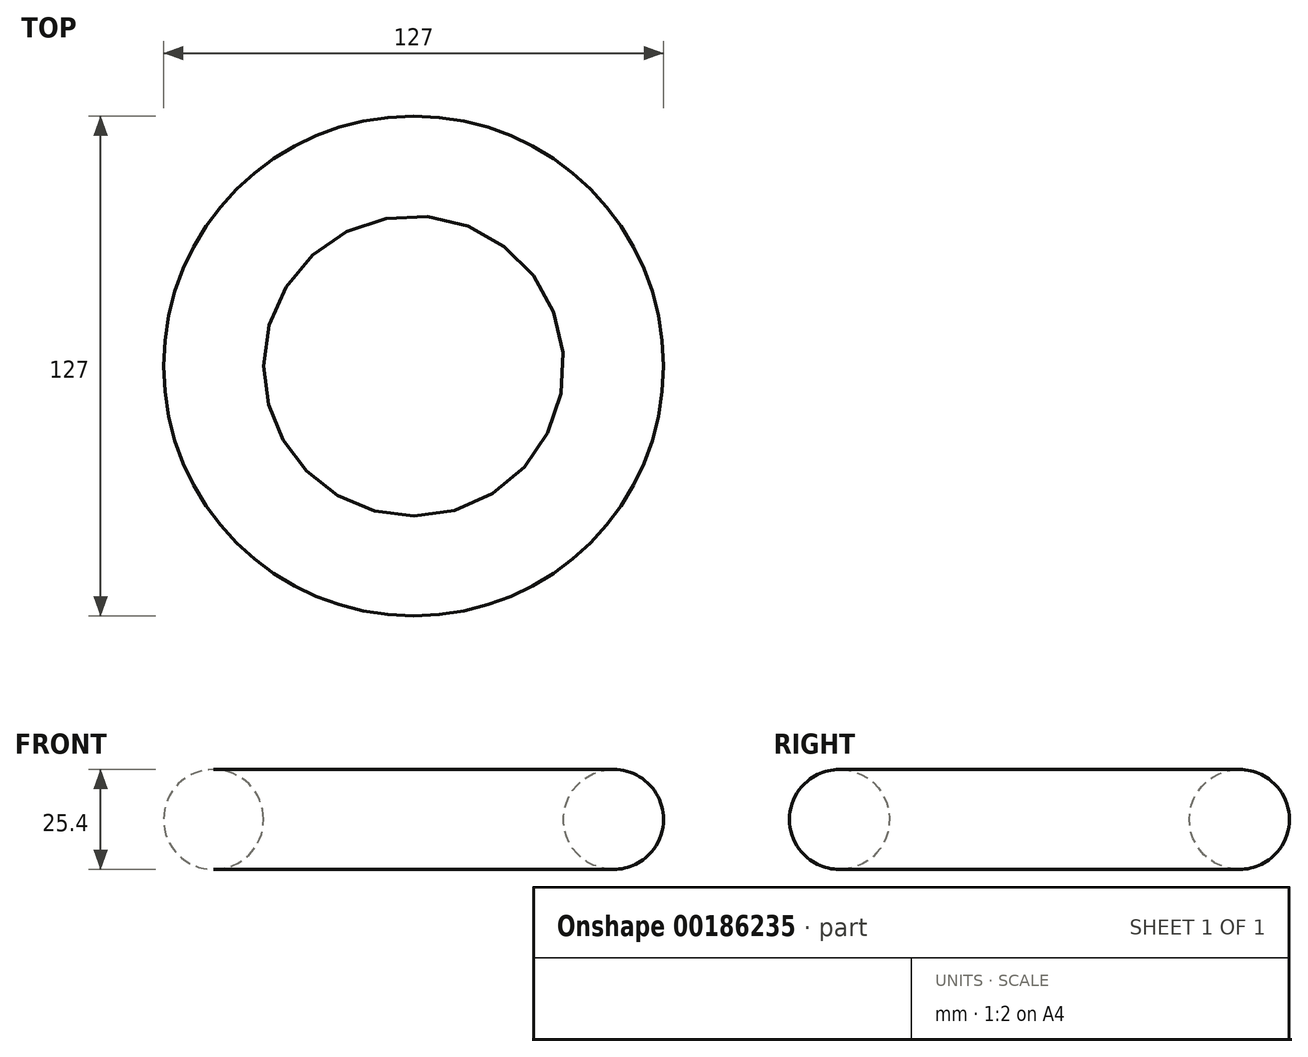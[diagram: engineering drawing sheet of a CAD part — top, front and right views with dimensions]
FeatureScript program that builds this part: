
annotation { "Feature Type Name" : "Feature", "Feature Type Description" : "" }
export const myFeature = defineFeature(function(context is Context, id is Id, definition is map)
    precondition{}
    {
        {
            var Q0;
            Q0=qCreatedBy(makeId("Front.planeOp"),FACE);
            var sketch = newSketch(context, id + "F0", { "sketchPlane" : qUnion([Q0])});
            skCircle(sketch, "E0", {"center": v(50.8, 0) * mm, "radius": 12.7 * mm});
            skLineSegment(sketch, "E1", {"start": v(0, 0) * mm, "end": v(0, 35.67) * mm});
            skSolve(sketch);
        }
        {
            var Q0;
            Q0=makeQuery(id+"F0.imprint","IMPRINT",FACE,{"disambiguationData":[TD([[makeQuery(id+"F0.imprint","IMPRINT",EDGE,{"derivedFrom":sQuery(id+"F0.wireOp",EDGE,"E0")}),1.0]])]});
            var Q1;
            Q1=sQuery(id+"F0.wireOp",EDGE,"E1");
            revolve(context, id + "F1", {"entities" : qUnion([Q0]), "axis" : qUnion([Q1]), "revolveType" : RevolveType.FULL});
        }
    });
